# Revit family: Theia-2
name_source: partatom
category: Furniture
units: mm (PartAtom-declared; Revit-internal decimal feet)

## family parameters
Always vertical = Yes
Cut with Voids When Loaded = No
OmniClass Number = 23.40.00.00
OmniClass Title = Equipment and Furnishings
Room Calculation Point = No
Shared = No
Work Plane-Based = No

## types (4) — shared parameters
Assembly Code = E2020200
Frame = Gresham - Chrome
Manufacturer = Gresham Office Funiture
Model = THEIA
Plastic Foot = Gresham - Plastic Foot
Product Brochure = https://gof.co.uk
Product Data Specification = https://gof.co.uk
Range = SEATING
Seat = Gresham - Theia Grey Plastic
Seat Pad = Gresham - Camira  Trail - HTL05
URL = www.gof.co.uk

## per-type parameters (varying)
| type | Arms | Product Code | Seat Pad (Vis) |
| EIA | Yes | EIA | No |
| EI1 | No | EI1 | No |
| EI1SP | No | EI1SP | Yes |
| EIASP | Yes | EI1SP | Yes |

## geometry (parser evidence)
native form markers: Sweep x2
no freeform markers — native parametric forms only
